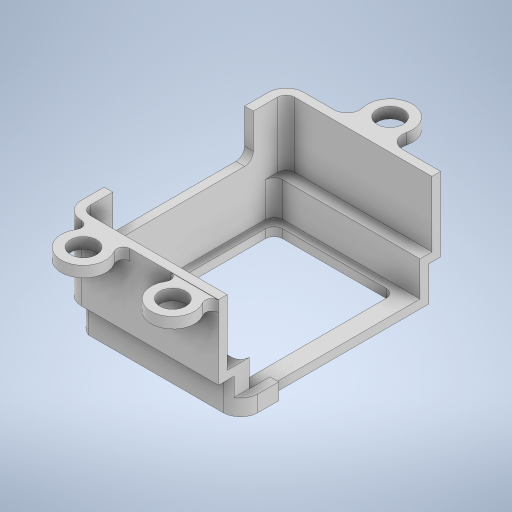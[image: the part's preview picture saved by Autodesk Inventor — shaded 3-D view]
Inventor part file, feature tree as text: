
AUTODESK INVENTOR PART (.ipt)
format: ipt  version: 2023 (Build 270158000, 158)  size: 475,136 bytes
history: native  units: in
note: dims shown in document units (in); Inventor stores cm internally (conversion verified against a paired STEP export)
features: extrude x8, sketch x4, projected_geometry x2, plane x1
ambient origin geometry x8: Origin, YZ Plane, XZ Plane, XY Plane, X Axis, Y Axis, Z Axis, Center Point
bodies: Body1 (feature_tree)
feature tree (15):
  extrude  "Extrusion3"  Depth=0.0787in
  plane  "Work Plane1"
  extrude  "Extrusion4"  Depth=0.315in TaperAngle=0.0deg
  sketch  "Sketch2"  dims[d8=0.0787in d9=0.0787in]
  extrude  "Extrusion7"  Depth=0.0787in
  extrude  "Extrusion8"  Depth=1.2402in
  extrude  "Extrusion10"  Depth=1.2402in
  extrude  "Extrusion11"  Depth=1.2402in
  extrude  "Extrusion12"  Depth=0.0787in TaperAngle=0.0deg
  extrude  "Extrusion13"  Depth=0.5906in TaperAngle=0.0deg
  projected_geometry  "Projected Loop1"
  sketch  "Sketch5"  dims[d10=0.0787in d11=0.0in d12=0.315in d13=0.0in]
  sketch  "Sketch6"  dims[d14=0.315in d19=0.0787in]
  projected_geometry  "Projected Loop3"
  sketch  "Sketch8"  dims[d20=0.0787in d21=1.2402in d22=1.2402in d23=1.2402in d28=0.0787in d29=0.0in d30=0.5906in d31=0.0in d34=0.4035in d35=0.2362in d38=0.1181in d39=0.1181in d40=0.3937in d41=0.2362in d42=0.1181in d43=0.1181in d44=0.4035in d45=0.2362in d46=0.1181in d47=0.1181in d49=0.8071in d50=0.0984in d51=0.0in d52=0.1575in d53=1.4744in d54=1.0925in d55=0.1575in d56=0.0787in d57=0.0787in d58=0.0in d59=0.0787in d61=1.2697in d62=1.6929in d64=0.2461in d65=0.0in d66=0.0787in d67=0.0787in d68=0.187in d69=0.1673in d70=0.2461in d71=0.0in]
